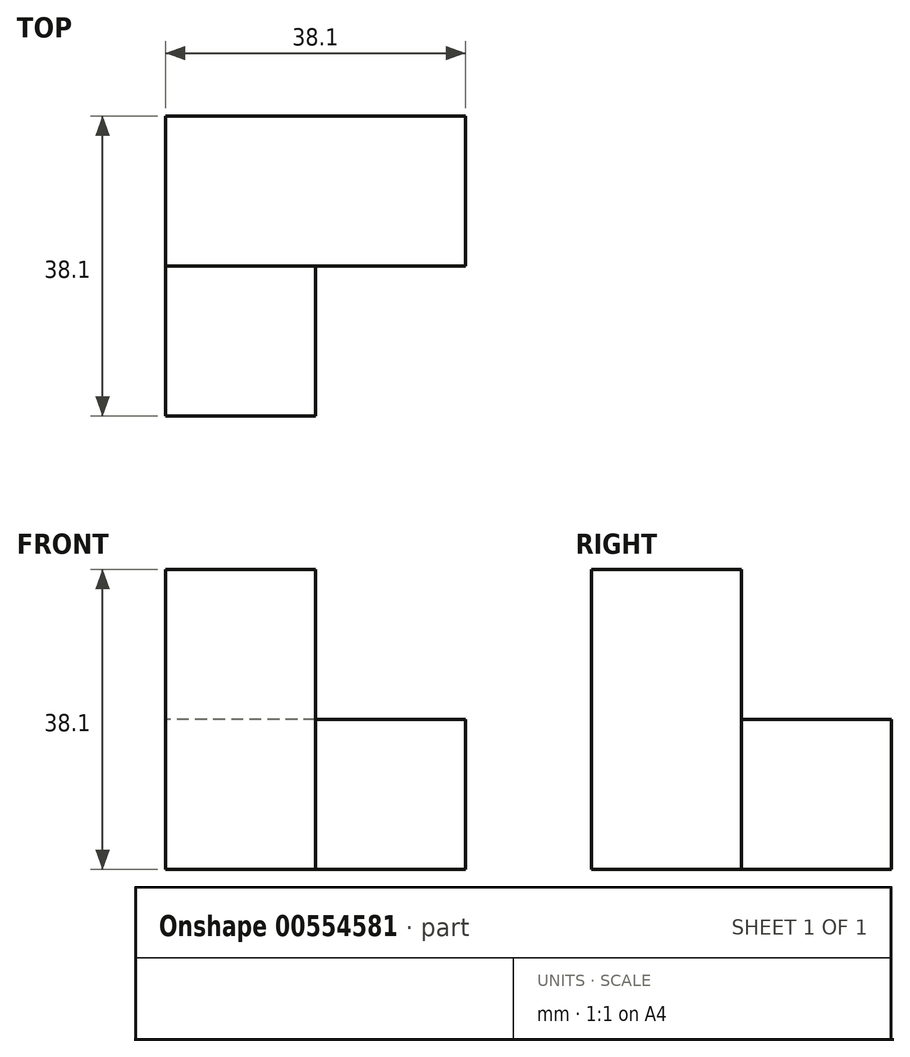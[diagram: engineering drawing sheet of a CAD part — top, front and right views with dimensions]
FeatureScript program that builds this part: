
annotation { "Feature Type Name" : "Feature", "Feature Type Description" : "" }
export const myFeature = defineFeature(function(context is Context, id is Id, definition is map)
    precondition{}
    {
        {
            var Q0;
            Q0=qCreatedBy(makeId("Right.planeOp"),FACE);
            var sketch = newSketch(context, id + "F0", { "sketchPlane" : qUnion([Q0])});
            skLineSegment(sketch, "E0", {"start": v(-36.79, 11.33) * mm, "end": v(-17.74, 11.33) * mm});
            skLineSegment(sketch, "E1", {"start": v(-17.74, 11.33) * mm, "end": v(-17.74, -7.72) * mm});
            skLineSegment(sketch, "E2", {"start": v(-17.74, -7.72) * mm, "end": v(1.31, -7.72) * mm});
            skLineSegment(sketch, "E3", {"start": v(1.31, -7.72) * mm, "end": v(1.31, -26.77) * mm});
            skLineSegment(sketch, "E4", {"start": v(1.31, -26.77) * mm, "end": v(-17.74, -26.77) * mm});
            skLineSegment(sketch, "E5", {"start": v(-17.74, -26.77) * mm, "end": v(-36.79, -26.77) * mm});
            skLineSegment(sketch, "E6", {"start": v(-36.79, -26.77) * mm, "end": v(-36.79, 11.33) * mm});
            skLineSegment(sketch, "E7", {"start": v(-17.74, -26.77) * mm, "end": v(-17.74, -7.72) * mm});
            skSolve(sketch);
        }
        {
            var Q0;
            Q0=makeQuery(id+"F0.imprint","IMPRINT",FACE,{"disambiguationData":[TD([[makeQuery(id+"F0.imprint","IMPRINT",EDGE,{"derivedFrom":sQuery(id+"F0.wireOp",EDGE,"E0")}),-1.0]])]});
            extrude(context, id + "F1", {"entities" : qUnion([Q0]), "depth" : 19.05 * mm, "offsetDistance" : 25.4 * mm});
        }
        {
            var Q0;
            Q0=makeQuery(id+"F0.imprint","IMPRINT",FACE,{"disambiguationData":[TD([[makeQuery(id+"F0.imprint","IMPRINT",EDGE,{"derivedFrom":sQuery(id+"F0.wireOp",EDGE,"E2")}),-1.0]])]});
            extrude(context, id + "F2", {"entities" : qUnion([Q0]), "operationType" : NewBodyOperationType.ADD, "depth" : 38.1 * mm, "offsetDistance" : 25.4 * mm});
        }
    });
